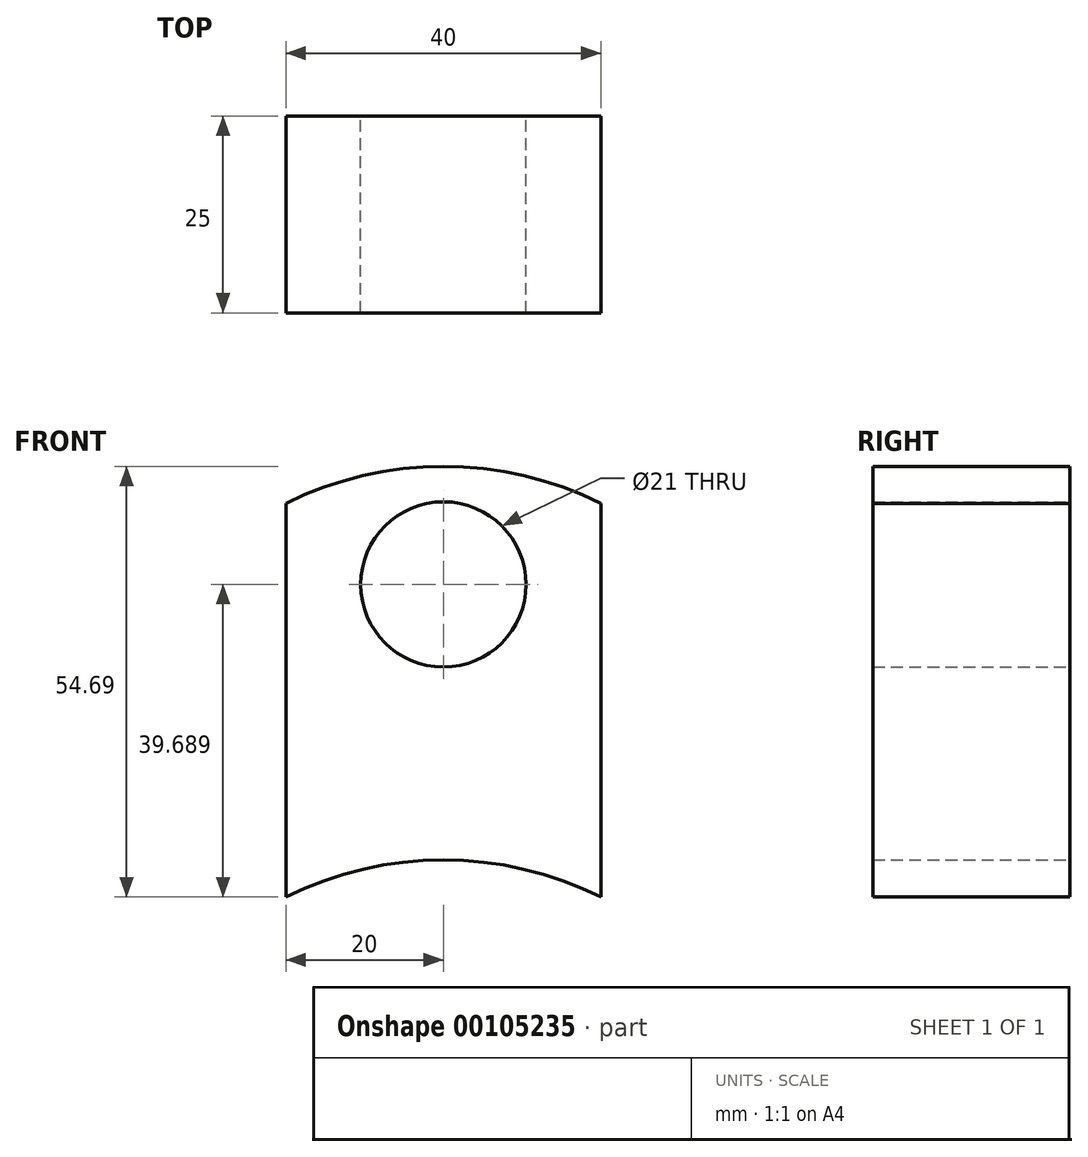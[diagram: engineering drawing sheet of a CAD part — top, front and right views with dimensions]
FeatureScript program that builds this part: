
annotation { "Feature Type Name" : "Feature", "Feature Type Description" : "" }
export const myFeature = defineFeature(function(context is Context, id is Id, definition is map)
    precondition{}
    {
        {
            var Q0;
            Q0=qCreatedBy(makeId("Front.planeOp"),FACE);
            var sketch = newSketch(context, id + "F0", { "sketchPlane" : qUnion([Q0])});
            skLineSegment(sketch, "E0", {"start": v(0, 0) * mm, "end": v(40, 0) * mm});
            skLineSegment(sketch, "E1", {"start": v(40, 0) * mm, "end": v(40, 50) * mm});
            skLineSegment(sketch, "E2", {"start": v(40, 50) * mm, "end": v(0, 50) * mm});
            skLineSegment(sketch, "E3", {"start": v(0, 50) * mm, "end": v(0, 0) * mm});
            skCircle(sketch, "E4", {"center": v(20, 39.69) * mm, "radius": 10.5 * mm});
            skArc(sketch, "E5", {"start": v(40, 50) * mm, "mid": v(20, 54.69) * mm, "end": v(0, 50) * mm});
            skArc(sketch, "E6", {"start": v(40, 0) * mm, "mid": v(20, 4.69) * mm, "end": v(0, 0) * mm});
            skSolve(sketch);
        }
        {
            var Q0;
            {var subQ5=sQuery(id+"F0.wireOp",EDGE,"E1");Q0=makeQuery(id+"F0.imprint","IMPRINT",FACE,{"disambiguationData":[TD([[makeQuery(id+"F0.imprint","IMPRINT",EDGE,{"derivedFrom":subQ5}),1.0]])]});}
            var Q1;
            {var subQ0=sQuery(id+"F0.wireOp",EDGE,"E5");Q1=makeQuery(id+"F0.imprint","IMPRINT",FACE,{"disambiguationData":[TD([[makeQuery(id+"F0.imprint","IMPRINT",EDGE,{"derivedFrom":subQ0}),1.0]])]});}
            extrude(context, id + "F1", {"entities" : qUnion([Q0, Q1]), "depth" : 25 * mm});
        }
    });
